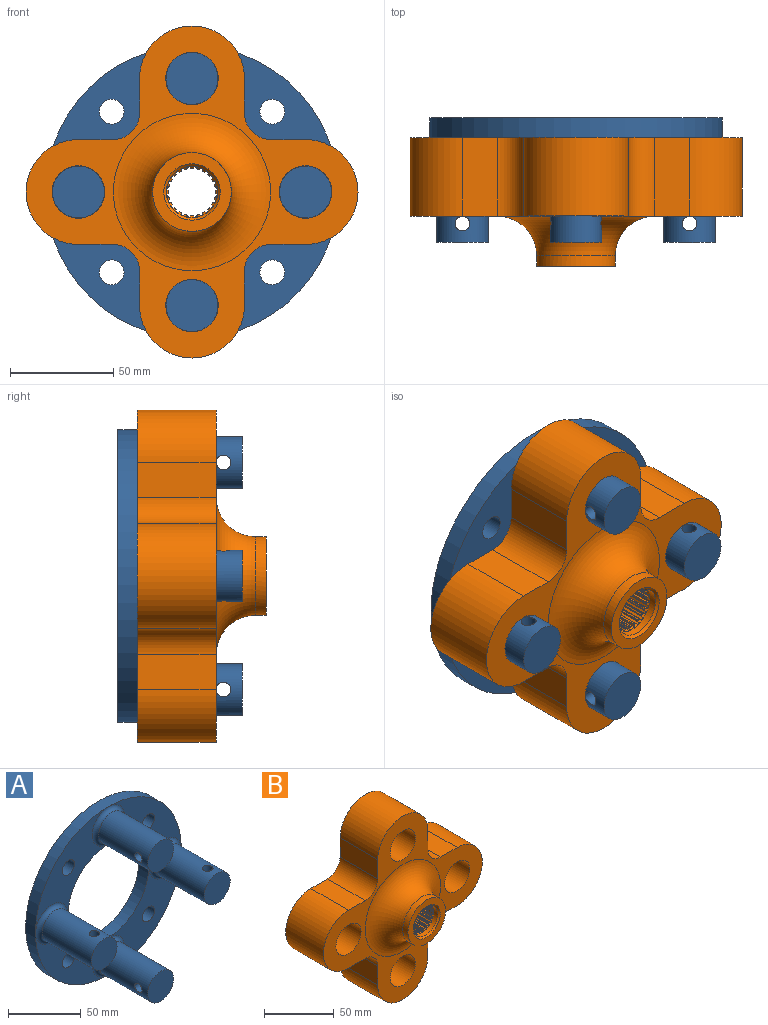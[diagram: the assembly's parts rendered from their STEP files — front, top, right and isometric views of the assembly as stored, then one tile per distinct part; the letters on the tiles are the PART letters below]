
ASSEMBLY  parts=2 mates=1
PART A: 24 faces, bbox 149x60.3x149 mm
  f0: cylinder r=39.12mm len=78.25mm, axis (0,1,0), area 2341.5mm2, adj f6,f7
  f1: cylinder r=6mm len=12mm, axis (0,1,0), area 359.1mm2, adj f6,f7
  f2: cylinder r=6mm len=12mm, axis (0,1,0), area 359.1mm2, adj f6,f7
  f3: cylinder r=6mm len=12mm, axis (0,1,0), area 359.1mm2, adj f6,f7
  f4: cylinder r=6mm len=12mm, axis (0,1,0), area 359.1mm2, adj f6,f7
  f5: cylinder r=70.88mm len=141.75mm, axis (0,1,0), area 4241.7mm2, adj f6,f7
  f6: plane 141.75x141.75mm, normal (0,-1,0), area 7403.2mm2, adj f0,f1,f2,f3,f4,f5,f20,f21
  f7: plane 141.75x141.75mm, normal (0,1,0), area 10519.6mm2, adj f0,f1,f2,f3,f4,f5
  f8: cylinder r=12.57mm len=47.63mm, axis (0,1,0), area 3681.2mm2, adj f9,f17,f23
  f9: plane 25.15x25.15mm, normal (0,-1,0), area 496.6mm2, adj f8
  f10: cylinder r=12.57mm len=47.63mm, axis (0,1,0), area 3681.3mm2, adj f11,f19,f22
  f11: plane 25.15x25.15mm, normal (0,-1,0), area 496.6mm2, adj f10
  f12: cylinder r=12.57mm len=47.63mm, axis (0,1,0), area 3681.2mm2, adj f13,f16,f21
  f13: plane 25.15x25.15mm, normal (0,-1,0), area 496.6mm2, adj f12
  f14: cylinder r=12.57mm len=47.63mm, axis (0,1,0), area 3681.3mm2, adj f15,f18,f20
  f15: plane 25.15x25.15mm, normal (0,-1,0), area 496.6mm2, adj f14
  f16: cylinder r=3.57mm len=25.15mm, axis (1,0,0), area 552.8mm2, adj f12
  f17: cylinder r=3.57mm len=25.15mm, axis (1,0,0), area 552.8mm2, adj f8
  f18: cylinder r=3.57mm len=25.15mm, axis (0,0,1), area 552.8mm2, adj f14
  f19: cylinder r=3.57mm len=25.15mm, axis (0,0,1), area 552.8mm2, adj f10
  f20: torus R=15.75mm, axis (0,-1,0), area 430.1mm2, adj f6,f14
  f21: torus R=15.75mm, axis (0,-1,0), area 430.1mm2, adj f6,f12
  f22: torus R=15.75mm, axis (0,-1,0), area 430.1mm2, adj f6,f10
  f23: torus R=15.75mm, axis (0,-1,0), area 430.1mm2, adj f6,f8
PART B: 178 faces, bbox 160.8x62.4x160.8 mm
  f0: plane 53.34x53.34mm, normal (0,1,0), area 1796.6mm2, adj f31,f34,f35,f36,f37,f38,f39,f40
  f1: cone r=9.84mm half-angle=45deg, axis (0,-1,0), area 61.6mm2, adj f32,f34,f35,f36,f37,f38,f39,f40
  f2: cylinder r=12.7mm len=38.1mm, axis (0,1,0), area 760.1mm2, adj f3,f20,f22,f23
  f3: plane 38.1x16.9mm, normal (1,0,0), area 643.9mm2, adj f2,f4,f22,f23
  f4: cylinder r=25.4mm len=50.8mm, axis (0,1,0), area 3040.2mm2, adj f3,f5,f22,f23
  f5: plane 38.1x16.9mm, normal (-1,0,0), area 643.9mm2, adj f4,f6,f22,f23
  f6: cylinder r=12.7mm len=38.1mm, axis (0,1,0), area 760.1mm2, adj f5,f7,f22,f23
  f7: plane 38.1x16.9mm, normal (0,0,1), area 643.9mm2, adj f6,f8,f22,f23
  f8: cylinder r=25.4mm len=50.8mm, axis (0,1,0), area 3040.2mm2, adj f7,f9,f22,f23
  f9: plane 38.1x16.9mm, normal (0,0,-1), area 643.9mm2, adj f8,f10,f22,f23
  f10: cylinder r=12.7mm len=38.1mm, axis (0,1,0), area 760.1mm2, adj f9,f11,f22,f23
  f11: plane 38.1x16.9mm, normal (-1,0,0), area 643.9mm2, adj f10,f12,f22,f23
  f12: cylinder r=25.4mm len=50.8mm, axis (0,1,0), area 3040.2mm2, adj f11,f13,f22,f23
  f13: plane 38.1x16.9mm, normal (1,0,0), area 643.9mm2, adj f12,f14,f22,f23
  f14: cylinder r=12.7mm len=38.1mm, axis (0,1,0), area 760.1mm2, adj f13,f15,f22,f23
  f15: plane 38.1x16.9mm, normal (0,0,-1), area 643.9mm2, adj f14,f16,f22,f23
  f16: cylinder r=25.4mm len=50.8mm, axis (0,1,0), area 3040.2mm2, adj f15,f20,f22,f23
  f17: cylinder r=12.7mm len=34.93mm, axis (0,1,0), area 2786.9mm2, adj f22,f27
  f18: cylinder r=12.7mm len=34.93mm, axis (0,1,0), area 2786.9mm2, adj f22,f30
  f19: cylinder r=12.7mm len=34.93mm, axis (0,1,0), area 2786.9mm2, adj f22,f29
  f20: plane 38.1x16.9mm, normal (0,0,1), area 643.9mm2, adj f2,f16,f22,f23
  f21: cylinder r=12.7mm len=34.93mm, axis (0,1,0), area 2786.9mm2, adj f22,f28
  f22: plane 160.8x160.8mm, normal (0,-1,0), area 6200.3mm2, adj f2,f3,f4,f5,f6,f7,f8,f9
  f23: plane 160.8x160.8mm, normal (0,1,0), area 6474.3mm2, adj f2,f3,f4,f5,f6,f7,f8,f9
  f24: cylinder r=19.05mm len=38.1mm, axis (0,1,0), area 621.2mm2, adj f25,f26
  f25: plane 38.1x38.1mm, normal (0,-1,0), area 554.5mm2, adj f24,f33
  f26: torus R=38.1mm, axis (0,-1,0), area 4883.2mm2, adj f22,f24
  f27: cone r=15.88mm half-angle=45deg, axis (0,1,0), area 403.1mm2, adj f17,f23
  f28: cone r=15.88mm half-angle=45deg, axis (0,1,0), area 403.1mm2, adj f21,f23
  f29: cone r=15.88mm half-angle=45deg, axis (0,1,0), area 403.1mm2, adj f19,f23
  f30: cone r=15.88mm half-angle=45deg, axis (0,1,0), area 403.1mm2, adj f18,f23
  f31: cone r=26.67mm half-angle=21.8deg, axis (0,1,0), area 2454.6mm2, adj f0,f23
  f32: cylinder r=12.38mm len=24.77mm, axis (0,-1,0), area 296.4mm2, adj f1,f33
  f33: cone r=12.38mm half-angle=45deg, axis (0,-1,0), area 146.9mm2, adj f25,f32
  f34: cylinder r=12.2mm len=44.64mm, axis (0,-1,0), area 53.4mm2, adj f0,f1,f35,f175
  f35: plane 44.65x0.66mm, normal (0.87,0,-0.5), area 33.3mm2, adj f0,f1,f34,f39
  f36: cylinder r=11.39mm len=43.83mm, axis (0,-1,0), area 34.5mm2, adj f0,f1,f39,f40
  f37: plane 44.65x0.66mm, normal (-0.87,0,-0.5), area 33.3mm2, adj f0,f1,f38,f40
  f38: cylinder r=12.2mm len=44.64mm, axis (0,-1,0), area 53.4mm2, adj f0,f1,f37,f41
  f39: cylinder r=0.25mm len=43.97mm, axis (0,-1,0), area 12.1mm2, adj f0,f1,f35,f36
  f40: cylinder r=0.25mm len=43.97mm, axis (0,-1,0), area 12.1mm2, adj f0,f1,f36,f37
  f41: plane 44.65x0.74mm, normal (0.97,0,-0.26), area 33.3mm2, adj f0,f1,f38,f45
  f42: cylinder r=11.39mm len=43.83mm, axis (0,-1,0), area 34.5mm2, adj f0,f1,f45,f46
  f43: plane 44.65x0.54mm, normal (-0.71,0,-0.71), area 33.3mm2, adj f0,f1,f44,f46
  f44: cylinder r=12.2mm len=44.64mm, axis (0,-1,0), area 53.4mm2, adj f0,f1,f43,f47
  f45: cylinder r=0.25mm len=43.97mm, axis (0,-1,0), area 12.1mm2, adj f0,f1,f41,f42
  f46: cylinder r=0.25mm len=43.97mm, axis (0,-1,0), area 12.1mm2, adj f0,f1,f42,f43
  f47: plane 44.65x0.76mm, normal (1,0,0), area 33.3mm2, adj f0,f1,f44,f51
  f48: cylinder r=11.39mm len=43.83mm, axis (0,-1,0), area 34.5mm2, adj f0,f1,f51,f52
  f49: plane 44.65x0.66mm, normal (-0.5,0,-0.87), area 33.3mm2, adj f0,f1,f50,f52
  f50: cylinder r=12.2mm len=44.64mm, axis (0,-1,0), area 53.4mm2, adj f0,f1,f49,f53
  f51: cylinder r=0.25mm len=43.97mm, axis (0,-1,0), area 12.1mm2, adj f0,f1,f47,f48
  f52: cylinder r=0.25mm len=43.97mm, axis (0,-1,0), area 12.1mm2, adj f0,f1,f48,f49
  f53: plane 44.65x0.74mm, normal (0.97,0,0.26), area 33.3mm2, adj f0,f1,f50,f57
  f54: cylinder r=11.39mm len=43.83mm, axis (0,-1,0), area 34.5mm2, adj f0,f1,f57,f58
  f55: plane 44.65x0.74mm, normal (-0.26,0,-0.97), area 33.3mm2, adj f0,f1,f56,f58
  f56: cylinder r=12.2mm len=44.64mm, axis (0,-1,0), area 53.4mm2, adj f0,f1,f55,f59
  f57: cylinder r=0.25mm len=43.97mm, axis (0,-1,0), area 12.1mm2, adj f0,f1,f53,f54
  f58: cylinder r=0.25mm len=43.97mm, axis (0,-1,0), area 12.1mm2, adj f0,f1,f54,f55
  f59: plane 44.65x0.66mm, normal (0.87,0,0.5), area 33.3mm2, adj f0,f1,f56,f63
  f60: cylinder r=11.39mm len=43.83mm, axis (0,-1,0), area 34.5mm2, adj f0,f1,f63,f64
  f61: plane 44.65x0.76mm, normal (0,0,-1), area 33.3mm2, adj f0,f1,f62,f64
  f62: cylinder r=12.2mm len=44.64mm, axis (0,-1,0), area 53.4mm2, adj f0,f1,f61,f65
  f63: cylinder r=0.25mm len=43.97mm, axis (0,-1,0), area 12.1mm2, adj f0,f1,f59,f60
  f64: cylinder r=0.25mm len=43.97mm, axis (0,-1,0), area 12.1mm2, adj f0,f1,f60,f61
  f65: plane 44.65x0.54mm, normal (0.71,0,0.71), area 33.3mm2, adj f0,f1,f62,f69
  f66: cylinder r=11.39mm len=43.83mm, axis (0,-1,0), area 34.5mm2, adj f0,f1,f69,f70
  f67: plane 44.65x0.74mm, normal (0.26,0,-0.97), area 33.3mm2, adj f0,f1,f68,f70
  f68: cylinder r=12.2mm len=44.64mm, axis (0,-1,0), area 53.4mm2, adj f0,f1,f67,f71
  f69: cylinder r=0.25mm len=43.97mm, axis (0,-1,0), area 12.1mm2, adj f0,f1,f65,f66
  f70: cylinder r=0.25mm len=43.97mm, axis (0,-1,0), area 12.1mm2, adj f0,f1,f66,f67
  f71: plane 44.65x0.66mm, normal (0.5,0,0.87), area 33.3mm2, adj f0,f1,f68,f75
  f72: cylinder r=11.39mm len=43.83mm, axis (0,-1,0), area 34.5mm2, adj f0,f1,f75,f76
  f73: plane 44.65x0.66mm, normal (0.5,0,-0.87), area 33.3mm2, adj f0,f1,f74,f76
  f74: cylinder r=12.2mm len=44.64mm, axis (0,-1,0), area 53.4mm2, adj f0,f1,f73,f77
  f75: cylinder r=0.25mm len=43.97mm, axis (0,-1,0), area 12.1mm2, adj f0,f1,f71,f72
  f76: cylinder r=0.25mm len=43.97mm, axis (0,-1,0), area 12.1mm2, adj f0,f1,f72,f73
  f77: plane 44.65x0.74mm, normal (0.26,0,0.97), area 33.3mm2, adj f0,f1,f74,f81
  f78: cylinder r=11.39mm len=43.83mm, axis (0,-1,0), area 34.5mm2, adj f0,f1,f81,f82
  f79: plane 44.65x0.54mm, normal (0.71,0,-0.71), area 33.3mm2, adj f0,f1,f80,f82
  f80: cylinder r=12.2mm len=44.64mm, axis (0,-1,0), area 53.4mm2, adj f0,f1,f79,f83
  f81: cylinder r=0.25mm len=43.97mm, axis (0,-1,0), area 12.1mm2, adj f0,f1,f77,f78
  f82: cylinder r=0.25mm len=43.97mm, axis (0,-1,0), area 12.1mm2, adj f0,f1,f78,f79
  f83: plane 44.65x0.76mm, normal (0,0,1), area 33.3mm2, adj f0,f1,f80,f87
  f84: cylinder r=11.39mm len=43.83mm, axis (0,-1,0), area 34.5mm2, adj f0,f1,f87,f88
  f85: plane 44.65x0.66mm, normal (0.87,0,-0.5), area 33.3mm2, adj f0,f1,f86,f88
  f86: cylinder r=12.2mm len=44.64mm, axis (0,-1,0), area 53.4mm2, adj f0,f1,f85,f89
  f87: cylinder r=0.25mm len=43.97mm, axis (0,-1,0), area 12.1mm2, adj f0,f1,f83,f84
  f88: cylinder r=0.25mm len=43.97mm, axis (0,-1,0), area 12.1mm2, adj f0,f1,f84,f85
  f89: plane 44.65x0.74mm, normal (-0.26,0,0.97), area 33.3mm2, adj f0,f1,f86,f93
  f90: cylinder r=11.39mm len=43.83mm, axis (0,-1,0), area 34.5mm2, adj f0,f1,f93,f94
  f91: plane 44.65x0.74mm, normal (0.97,0,-0.26), area 33.3mm2, adj f0,f1,f92,f94
  f92: cylinder r=12.2mm len=44.64mm, axis (0,-1,0), area 53.4mm2, adj f0,f1,f91,f95
  f93: cylinder r=0.25mm len=43.97mm, axis (0,-1,0), area 12.1mm2, adj f0,f1,f89,f90
  f94: cylinder r=0.25mm len=43.97mm, axis (0,-1,0), area 12.1mm2, adj f0,f1,f90,f91
  f95: plane 44.65x0.66mm, normal (-0.5,0,0.87), area 33.3mm2, adj f0,f1,f92,f99
  f96: cylinder r=11.39mm len=43.83mm, axis (0,-1,0), area 34.5mm2, adj f0,f1,f99,f100
  f97: plane 44.65x0.76mm, normal (1,0,0), area 33.3mm2, adj f0,f1,f98,f100
  f98: cylinder r=12.2mm len=44.64mm, axis (0,-1,0), area 53.4mm2, adj f0,f1,f97,f101
  f99: cylinder r=0.25mm len=43.97mm, axis (0,-1,0), area 12.1mm2, adj f0,f1,f95,f96
  f100: cylinder r=0.25mm len=43.97mm, axis (0,-1,0), area 12.1mm2, adj f0,f1,f96,f97
  f101: plane 44.65x0.54mm, normal (-0.71,0,0.71), area 33.3mm2, adj f0,f1,f98,f105
  f102: cylinder r=11.39mm len=43.83mm, axis (0,-1,0), area 34.5mm2, adj f0,f1,f105,f106
  f103: plane 44.65x0.74mm, normal (0.97,0,0.26), area 33.3mm2, adj f0,f1,f104,f106
  f104: cylinder r=12.2mm len=44.64mm, axis (0,-1,0), area 53.4mm2, adj f0,f1,f103,f107
  f105: cylinder r=0.25mm len=43.97mm, axis (0,-1,0), area 12.1mm2, adj f0,f1,f101,f102
  f106: cylinder r=0.25mm len=43.97mm, axis (0,-1,0), area 12.1mm2, adj f0,f1,f102,f103
  f107: plane 44.65x0.66mm, normal (-0.87,0,0.5), area 33.3mm2, adj f0,f1,f104,f111
  f108: cylinder r=11.39mm len=43.83mm, axis (0,-1,0), area 34.5mm2, adj f0,f1,f111,f112
  f109: plane 44.65x0.66mm, normal (0.87,0,0.5), area 33.3mm2, adj f0,f1,f110,f112
  f110: cylinder r=12.2mm len=44.64mm, axis (0,-1,0), area 53.4mm2, adj f0,f1,f109,f113
  f111: cylinder r=0.25mm len=43.97mm, axis (0,-1,0), area 12.1mm2, adj f0,f1,f107,f108
  f112: cylinder r=0.25mm len=43.97mm, axis (0,-1,0), area 12.1mm2, adj f0,f1,f108,f109
  f113: plane 44.65x0.74mm, normal (-0.97,0,0.26), area 33.3mm2, adj f0,f1,f110,f117
  f114: cylinder r=11.39mm len=43.83mm, axis (0,-1,0), area 34.5mm2, adj f0,f1,f117,f118
  f115: plane 44.65x0.54mm, normal (0.71,0,0.71), area 33.3mm2, adj f0,f1,f116,f118
  f116: cylinder r=12.2mm len=44.64mm, axis (0,-1,0), area 53.4mm2, adj f0,f1,f115,f119
  f117: cylinder r=0.25mm len=43.97mm, axis (0,-1,0), area 12.1mm2, adj f0,f1,f113,f114
  f118: cylinder r=0.25mm len=43.97mm, axis (0,-1,0), area 12.1mm2, adj f0,f1,f114,f115
  f119: plane 44.65x0.76mm, normal (-1,0,0), area 33.3mm2, adj f0,f1,f116,f123
  f120: cylinder r=11.39mm len=43.83mm, axis (0,-1,0), area 34.5mm2, adj f0,f1,f123,f124
  f121: plane 44.65x0.66mm, normal (0.5,0,0.87), area 33.3mm2, adj f0,f1,f122,f124
  f122: cylinder r=12.2mm len=44.64mm, axis (0,-1,0), area 53.4mm2, adj f0,f1,f121,f125
  f123: cylinder r=0.25mm len=43.97mm, axis (0,-1,0), area 12.1mm2, adj f0,f1,f119,f120
  f124: cylinder r=0.25mm len=43.97mm, axis (0,-1,0), area 12.1mm2, adj f0,f1,f120,f121
  f125: plane 44.65x0.74mm, normal (-0.97,0,-0.26), area 33.3mm2, adj f0,f1,f122,f129
  f126: cylinder r=11.39mm len=43.83mm, axis (0,-1,0), area 34.5mm2, adj f0,f1,f129,f130
  f127: plane 44.65x0.74mm, normal (0.26,0,0.97), area 33.3mm2, adj f0,f1,f128,f130
  f128: cylinder r=12.2mm len=44.64mm, axis (0,-1,0), area 53.4mm2, adj f0,f1,f127,f131
  f129: cylinder r=0.25mm len=43.97mm, axis (0,-1,0), area 12.1mm2, adj f0,f1,f125,f126
  f130: cylinder r=0.25mm len=43.97mm, axis (0,-1,0), area 12.1mm2, adj f0,f1,f126,f127
  f131: plane 44.65x0.66mm, normal (-0.87,0,-0.5), area 33.3mm2, adj f0,f1,f128,f135
  f132: cylinder r=11.39mm len=43.83mm, axis (0,-1,0), area 34.5mm2, adj f0,f1,f135,f136
  f133: plane 44.65x0.76mm, normal (0,0,1), area 33.3mm2, adj f0,f1,f134,f136
  f134: cylinder r=12.2mm len=44.64mm, axis (0,-1,0), area 53.4mm2, adj f0,f1,f133,f137
  f135: cylinder r=0.25mm len=43.97mm, axis (0,-1,0), area 12.1mm2, adj f0,f1,f131,f132
  f136: cylinder r=0.25mm len=43.97mm, axis (0,-1,0), area 12.1mm2, adj f0,f1,f132,f133
  f137: plane 44.65x0.54mm, normal (-0.71,0,-0.71), area 33.3mm2, adj f0,f1,f134,f141
  f138: cylinder r=11.39mm len=43.83mm, axis (0,-1,0), area 34.5mm2, adj f0,f1,f141,f142
  f139: plane 44.65x0.74mm, normal (-0.26,0,0.97), area 33.3mm2, adj f0,f1,f140,f142
  f140: cylinder r=12.2mm len=44.64mm, axis (0,-1,0), area 53.4mm2, adj f0,f1,f139,f143
  f141: cylinder r=0.25mm len=43.97mm, axis (0,-1,0), area 12.1mm2, adj f0,f1,f137,f138
  f142: cylinder r=0.25mm len=43.97mm, axis (0,-1,0), area 12.1mm2, adj f0,f1,f138,f139
  f143: plane 44.65x0.66mm, normal (-0.5,0,-0.87), area 33.3mm2, adj f0,f1,f140,f147
  f144: cylinder r=11.39mm len=43.83mm, axis (0,-1,0), area 34.5mm2, adj f0,f1,f147,f148
  f145: plane 44.65x0.66mm, normal (-0.5,0,0.87), area 33.3mm2, adj f0,f1,f146,f148
  f146: cylinder r=12.2mm len=44.64mm, axis (0,-1,0), area 53.4mm2, adj f0,f1,f145,f149
  f147: cylinder r=0.25mm len=43.97mm, axis (0,-1,0), area 12.1mm2, adj f0,f1,f143,f144
  f148: cylinder r=0.25mm len=43.97mm, axis (0,-1,0), area 12.1mm2, adj f0,f1,f144,f145
  f149: plane 44.65x0.74mm, normal (-0.26,0,-0.97), area 33.3mm2, adj f0,f1,f146,f153
  f150: cylinder r=11.39mm len=43.83mm, axis (0,-1,0), area 34.5mm2, adj f0,f1,f153,f154
  f151: plane 44.65x0.54mm, normal (-0.71,0,0.71), area 33.3mm2, adj f0,f1,f152,f154
  f152: cylinder r=12.2mm len=44.64mm, axis (0,-1,0), area 53.4mm2, adj f0,f1,f151,f155
  f153: cylinder r=0.25mm len=43.97mm, axis (0,-1,0), area 12.1mm2, adj f0,f1,f149,f150
  f154: cylinder r=0.25mm len=43.97mm, axis (0,-1,0), area 12.1mm2, adj f0,f1,f150,f151
  f155: plane 44.65x0.76mm, normal (0,0,-1), area 33.3mm2, adj f0,f1,f152,f159
  f156: cylinder r=11.39mm len=43.83mm, axis (0,-1,0), area 34.5mm2, adj f0,f1,f159,f160
  f157: plane 44.65x0.66mm, normal (-0.87,0,0.5), area 33.3mm2, adj f0,f1,f158,f160
  f158: cylinder r=12.2mm len=44.64mm, axis (0,-1,0), area 53.4mm2, adj f0,f1,f157,f161
  f159: cylinder r=0.25mm len=43.97mm, axis (0,-1,0), area 12.1mm2, adj f0,f1,f155,f156
  f160: cylinder r=0.25mm len=43.97mm, axis (0,-1,0), area 12.1mm2, adj f0,f1,f156,f157
  f161: plane 44.65x0.74mm, normal (0.26,0,-0.97), area 33.3mm2, adj f0,f1,f158,f165
  f162: cylinder r=11.39mm len=43.83mm, axis (0,-1,0), area 34.5mm2, adj f0,f1,f165,f166
  f163: plane 44.65x0.74mm, normal (-0.97,0,0.26), area 33.3mm2, adj f0,f1,f164,f166
  f164: cylinder r=12.2mm len=44.64mm, axis (0,-1,0), area 53.4mm2, adj f0,f1,f163,f167
  f165: cylinder r=0.25mm len=43.97mm, axis (0,-1,0), area 12.1mm2, adj f0,f1,f161,f162
  f166: cylinder r=0.25mm len=43.97mm, axis (0,-1,0), area 12.1mm2, adj f0,f1,f162,f163
  f167: plane 44.65x0.66mm, normal (0.5,0,-0.87), area 33.3mm2, adj f0,f1,f164,f171
  f168: cylinder r=11.39mm len=43.83mm, axis (0,-1,0), area 34.5mm2, adj f0,f1,f171,f172
  f169: plane 44.65x0.76mm, normal (-1,0,0), area 33.3mm2, adj f0,f1,f170,f172
  f170: cylinder r=12.2mm len=44.64mm, axis (0,-1,0), area 53.4mm2, adj f0,f1,f169,f173
  f171: cylinder r=0.25mm len=43.97mm, axis (0,-1,0), area 12.1mm2, adj f0,f1,f167,f168
  f172: cylinder r=0.25mm len=43.97mm, axis (0,-1,0), area 12.1mm2, adj f0,f1,f168,f169
  f173: plane 44.65x0.54mm, normal (0.71,0,-0.71), area 33.3mm2, adj f0,f1,f170,f176
  f174: cylinder r=11.39mm len=43.83mm, axis (0,-1,0), area 34.5mm2, adj f0,f1,f176,f177
  f175: plane 44.65x0.74mm, normal (-0.97,0,-0.26), area 33.3mm2, adj f0,f1,f34,f177
  f176: cylinder r=0.25mm len=43.97mm, axis (0,-1,0), area 12.1mm2, adj f0,f1,f173,f174
  f177: cylinder r=0.25mm len=43.97mm, axis (0,-1,0), area 12.1mm2, adj f0,f1,f174,f175
PLACE A t=(120.18,21.2,20.23)mm
PLACE B t=(120.18,11.68,20.23)mm
MATE fastened A.f8 <-> B.f4  axis (0,-1,0) through (120.18,11.68,75.23)mm
